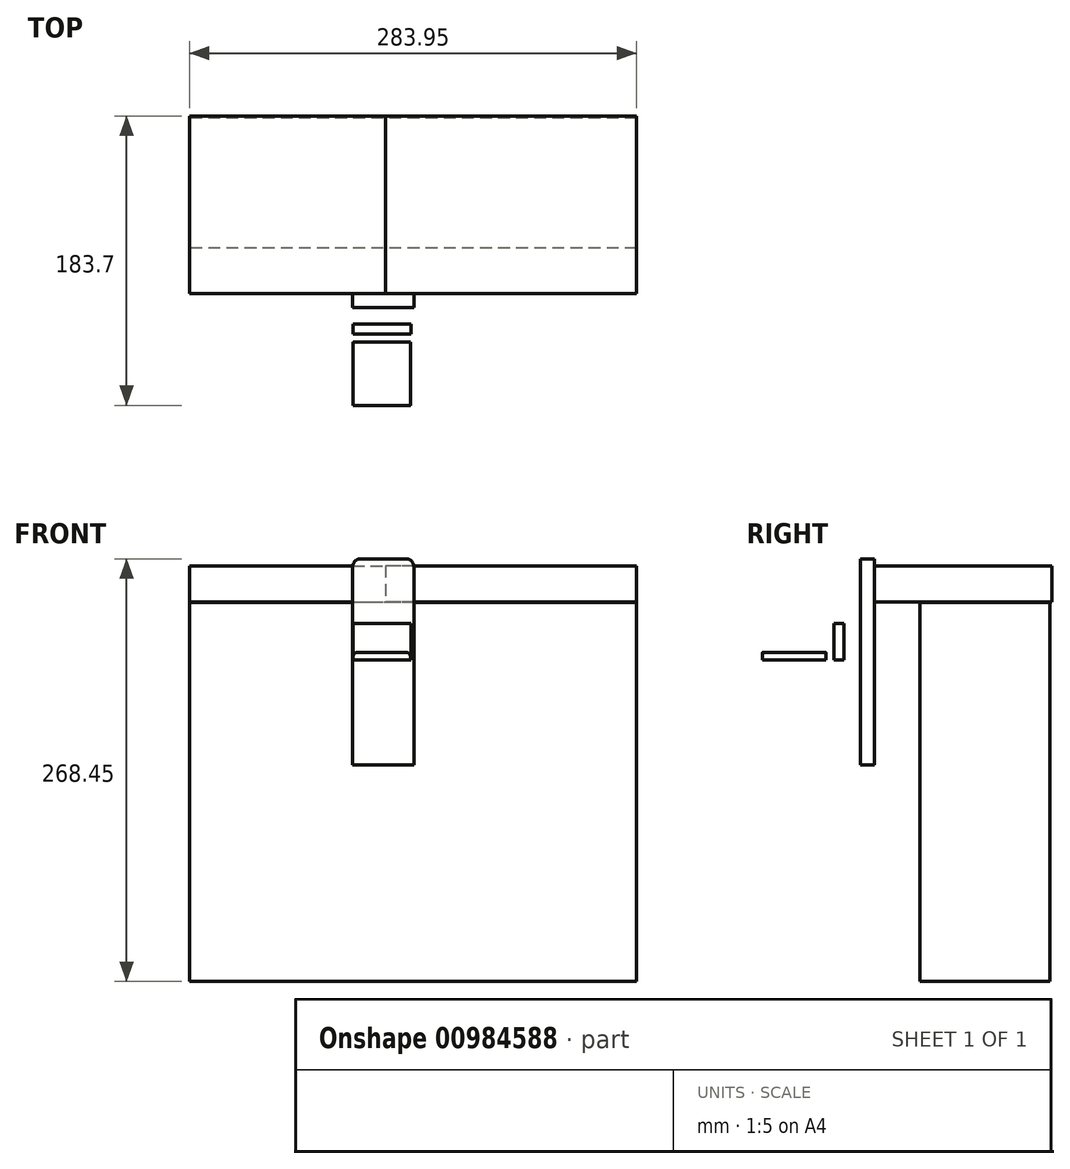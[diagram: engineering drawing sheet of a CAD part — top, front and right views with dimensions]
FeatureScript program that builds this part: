
annotation { "Feature Type Name" : "Feature", "Feature Type Description" : "" }
export const myFeature = defineFeature(function(context is Context, id is Id, definition is map)
    precondition{}
    {
        {
            var Q0;
            Q0=qCreatedBy(makeId("Front.planeOp"),FACE);
            var sketch = newSketch(context, id + "F0", { "sketchPlane" : qUnion([Q0])});
            skLineSegment(sketch, "E0.bottom", {"start": v(-20.93, 64.24) * mm, "end": v(17.86, 64.24) * mm});
            skLineSegment(sketch, "E0.top", {"start": v(-20.93, -66.76) * mm, "end": v(17.86, -66.76) * mm});
            skLineSegment(sketch, "E0.left", {"start": v(-20.93, 64.24) * mm, "end": v(-20.93, -66.76) * mm});
            skLineSegment(sketch, "E0.right", {"start": v(17.86, 64.24) * mm, "end": v(17.86, -66.76) * mm});
            skSolve(sketch);
        }
        {
            var Q0;
            Q0=makeQuery(id+"F0.imprint","IMPRINT",FACE,{"disambiguationData":[TD([[makeQuery(id+"F0.imprint","IMPRINT",EDGE,{"derivedFrom":sQuery(id+"F0.wireOp",EDGE,"E0.bottom")}),-1.0]])]});
            extrude(context, id + "F1", {"entities" : qUnion([Q0]), "depth" : 9.08 * mm, "offsetDistance" : 25.4 * mm});
        }
        {
            var Q0;
            Q0=qCreatedBy(makeId("Top.planeOp"),FACE);
            var sketch = newSketch(context, id + "F2", { "sketchPlane" : qUnion([Q0])});
            skLineSegment(sketch, "E1.bottom", {"start": v(-20.58, -19.34) * mm, "end": v(16.04, -19.34) * mm});
            skLineSegment(sketch, "E1.top", {"start": v(-20.58, -25.83) * mm, "end": v(16.04, -25.83) * mm});
            skLineSegment(sketch, "E1.left", {"start": v(-20.58, -19.34) * mm, "end": v(-20.58, -25.83) * mm});
            skLineSegment(sketch, "E1.right", {"start": v(16.04, -19.34) * mm, "end": v(16.04, -25.83) * mm});
            skSolve(sketch);
        }
        {
            var Q0;
            Q0=makeQuery(id+"F2.imprint","IMPRINT",FACE,{"disambiguationData":[TD([[makeQuery(id+"F2.imprint","IMPRINT",EDGE,{"derivedFrom":sQuery(id+"F2.wireOp",EDGE,"E1.bottom")}),-1.0]])]});
            extrude(context, id + "F3", {"entities" : qUnion([Q0]), "depth" : 23.3 * mm, "offsetDistance" : 25.4 * mm});
        }
        {
            var Q0;
            Q0=qCreatedBy(makeId("Top.planeOp"),FACE);
            var sketch = newSketch(context, id + "F4", { "sketchPlane" : qUnion([Q0])});
            skLineSegment(sketch, "E2.bottom", {"start": v(-20.57, -31.04) * mm, "end": v(15.7, -31.04) * mm});
            skLineSegment(sketch, "E2.top", {"start": v(-20.57, -71.1) * mm, "end": v(15.7, -71.1) * mm});
            skLineSegment(sketch, "E2.left", {"start": v(-20.57, -31.04) * mm, "end": v(-20.57, -71.1) * mm});
            skLineSegment(sketch, "E2.right", {"start": v(15.7, -31.04) * mm, "end": v(15.7, -71.1) * mm});
            skSolve(sketch);
        }
        {
            var Q0;
            Q0=makeQuery(id+"F4.imprint","IMPRINT",FACE,{"disambiguationData":[TD([[makeQuery(id+"F4.imprint","IMPRINT",EDGE,{"derivedFrom":sQuery(id+"F4.wireOp",EDGE,"E2.bottom")}),-1.0]])]});
            extrude(context, id + "F5", {"entities" : qUnion([Q0]), "depth" : 4.76 * mm, "offsetDistance" : 25.4 * mm});
        }
        {
            var Q0;
            Q0=makeQuery(id+"F5.opExtrude","CAP_EDGE",EDGE,{"disambiguationData":[OSD([sQuery(id+"F4.wireOp",EDGE,"E2.right")])],"isStart":false});
            var Q1;
            Q1=makeQuery(id+"F5.opExtrude","CAP_EDGE",EDGE,{"disambiguationData":[OSD([sQuery(id+"F4.wireOp",EDGE,"E2.left")])],"isStart":false});
            fillet(context, id + "F6", {"entities" : qUnion([Q0, Q1]), "radius" : 2.54 * mm, "tangentPropagation" : true, "allowEdgeOverflow" : false});
        }
        {
            var Q0;
            Q0=qCreatedBy(makeId("Right.planeOp"),FACE);
            var sketch = newSketch(context, id + "F7", { "sketchPlane" : qUnion([Q0])});
            skLineSegment(sketch, "E3.bottom", {"start": v(0, 59.73) * mm, "end": v(112.6, 59.73) * mm});
            skLineSegment(sketch, "E3.top", {"start": v(0, 36.81) * mm, "end": v(112.6, 36.81) * mm});
            skLineSegment(sketch, "E3.left", {"start": v(0, 59.73) * mm, "end": v(0, 36.81) * mm});
            skLineSegment(sketch, "E3.right", {"start": v(112.6, 59.73) * mm, "end": v(112.6, 36.81) * mm});
            skSolve(sketch);
        }
        {
            var Q0;
            Q0=qCreatedBy(makeId("Right.planeOp"),FACE);
            var sketch = newSketch(context, id + "F8", { "sketchPlane" : qUnion([Q0])});
            skLineSegment(sketch, "E4.bottom", {"start": v(28.87, 36.63) * mm, "end": v(111.33, 36.63) * mm});
            skLineSegment(sketch, "E4.top", {"start": v(28.87, -90.58) * mm, "end": v(111.33, -90.58) * mm});
            skLineSegment(sketch, "E4.left", {"start": v(28.87, 36.63) * mm, "end": v(28.87, -90.58) * mm});
            skLineSegment(sketch, "E4.right", {"start": v(111.33, 36.63) * mm, "end": v(111.33, -90.58) * mm});
            skSolve(sketch);
        }
        {
            var Q0;
            Q0 = qSketchRegion(id + "F7", true);
            var Q1;
            Q1=makeQuery(id+"F7.imprint","IMPRINT",FACE,{"disambiguationData":[TD([[makeQuery(id+"F7.imprint","IMPRINT",EDGE,{"derivedFrom":sQuery(id+"F7.wireOp",EDGE,"E3.bottom")}),-1.0]])]});
            var Q2;
            Q2 = qSketchRegion(id + "F8", true);
            extrude(context, id + "F9", {"entities" : qUnion([Q0, Q1, Q2]), "operationType" : NewBodyOperationType.ADD, "depth" : 159.42 * mm, "offsetDistance" : 25.4 * mm});
        }
        {
            var Q0;
            Q0=makeQuery(id+"F9.opExtrude","CAP_FACE",FACE,{"disambiguationData":[OSD([sQuery(id+"F8.wireOp",EDGE,"E4.bottom"),sQuery(id+"F8.wireOp",EDGE,"E4.top"),sQuery(id+"F8.wireOp",EDGE,"E4.left"),sQuery(id+"F8.wireOp",EDGE,"E4.right")])],"isStart":true});
            var Q1;
            Q1=makeQuery(id+"F9.opExtrude","CAP_FACE",FACE,{"disambiguationData":[OSD([sQuery(id+"F7.wireOp",EDGE,"E3.bottom"),sQuery(id+"F7.wireOp",EDGE,"E3.top"),sQuery(id+"F7.wireOp",EDGE,"E3.left"),sQuery(id+"F7.wireOp",EDGE,"E3.right")])],"isStart":true});
            extrude(context, id + "F10", {"entities" : qUnion([Q0, Q1]), "depth" : 124.53 * mm, "offsetDistance" : 25.4 * mm});
        }
        {
            var Q0;
            Q0=makeQuery(id+"F9.opExtrude","SWEPT_BODY",BODY,{"disambiguationData":[OSD([sQuery(id+"F8.wireOp",EDGE,"E4.bottom"),sQuery(id+"F8.wireOp",EDGE,"E4.top"),sQuery(id+"F8.wireOp",EDGE,"E4.left"),sQuery(id+"F8.wireOp",EDGE,"E4.right")])]});
            var Q1;
            Q1=makeQuery(id+"F10.opExtrude","SWEPT_BODY",BODY,{"disambiguationData":[OSD([sQuery(id+"F8.wireOp",EDGE,"E4.bottom"),sQuery(id+"F8.wireOp",EDGE,"E4.top"),sQuery(id+"F8.wireOp",EDGE,"E4.left"),sQuery(id+"F8.wireOp",EDGE,"E4.right")])]});
            booleanBodies(context, id + "F11", {"operationType" : BooleanOperationType.UNION, "tools" : qUnion([Q0, Q1])});
        }
        {
            var Q0;
            {var subQ0=sQuery(id+"F8.wireOp",EDGE,"E4.top");Q0=makeQuery(id+"F11.opBoolean","MERGE",FACE,{"derivedFrom":[makeQuery(id+"F9.opExtrude","SWEPT_FACE",FACE,{"disambiguationData":[OSD([subQ0])]}),makeQuery(id+"F10.opExtrude","SWEPT_FACE",FACE,{"disambiguationData":[OSD([subQ0])]})]});}
            extrude(context, id + "F12", {"entities" : qUnion([Q0]), "operationType" : NewBodyOperationType.ADD, "depth" : 113.62 * mm, "offsetDistance" : 25.4 * mm});
        }
        {
            var Q0;
            Q0=makeQuery(id+"F1.opExtrude","SWEPT_EDGE",EDGE,{"disambiguationData":[OSD([sQuery(id+"F0.wireOp",EDGE,"E0.bottom"),sQuery(id+"F0.wireOp",EDGE,"E0.right")])]});
            var Q1;
            Q1=makeQuery(id+"F1.opExtrude","SWEPT_EDGE",EDGE,{"disambiguationData":[OSD([sQuery(id+"F0.wireOp",EDGE,"E0.bottom"),sQuery(id+"F0.wireOp",EDGE,"E0.left")])]});
            fillet(context, id + "F13", {"entities" : qUnion([Q0, Q1]), "radius" : 5.08 * mm, "tangentPropagation" : true, "allowEdgeOverflow" : false});
        }
    });
